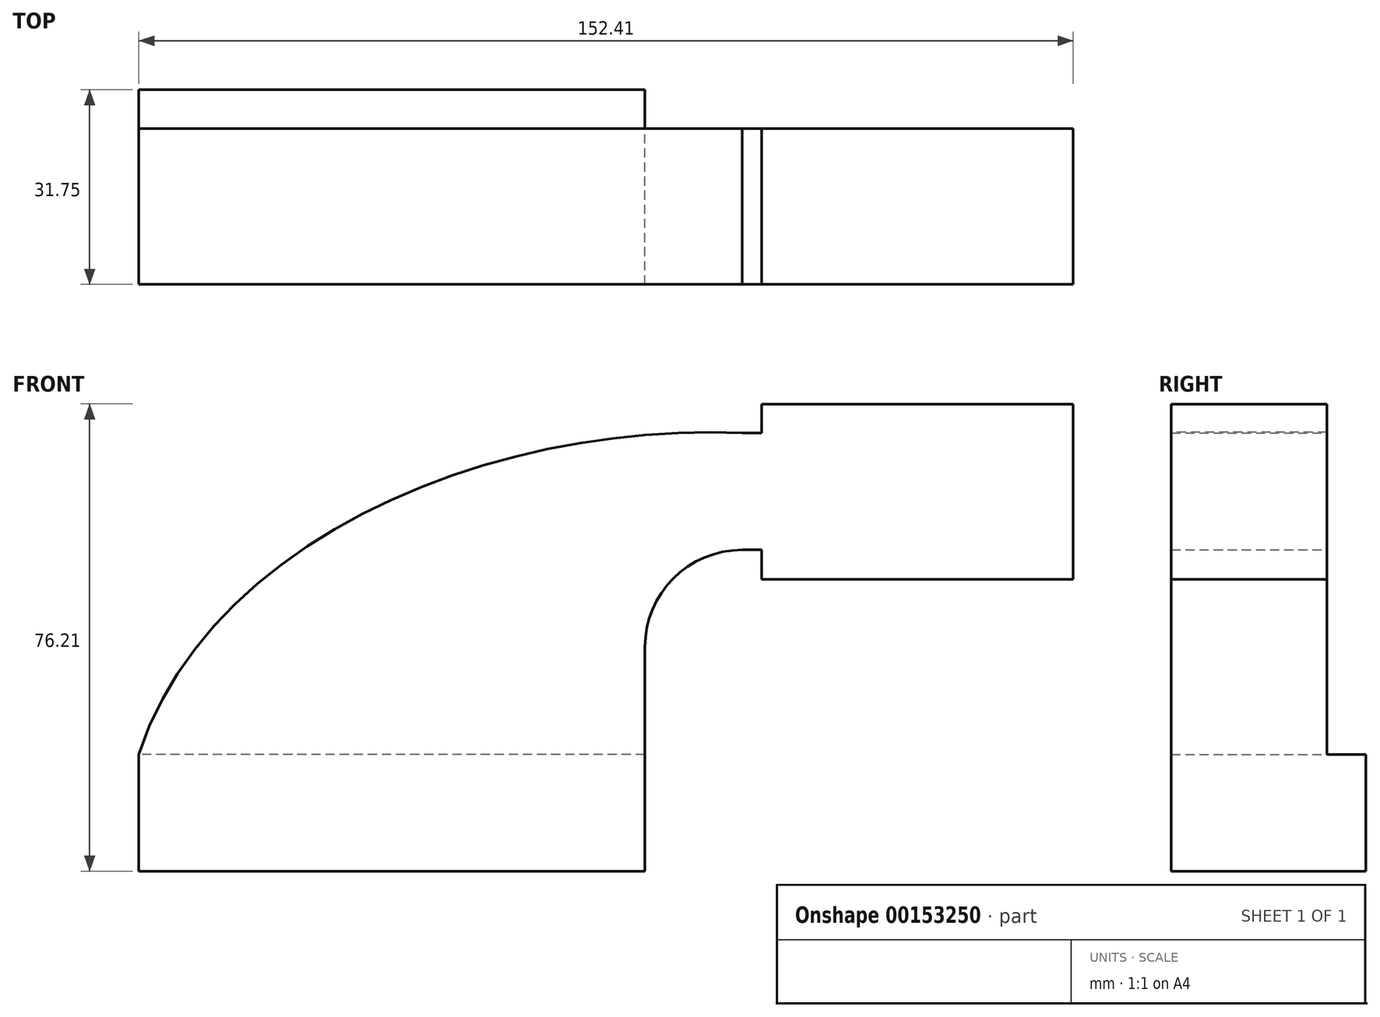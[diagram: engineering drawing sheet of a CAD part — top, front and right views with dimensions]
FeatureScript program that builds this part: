
annotation { "Feature Type Name" : "Feature", "Feature Type Description" : "" }
export const myFeature = defineFeature(function(context is Context, id is Id, definition is map)
    precondition{}
    {
        {
            var Q0;
            Q0=qCreatedBy(makeId("Front.planeOp"),FACE);
            var sketch = newSketch(context, id + "F0", { "sketchPlane" : qUnion([Q0])});
            skLineSegment(sketch, "E0.bottom", {"start": v(41.27, 9.53) * mm, "end": v(-41.28, 9.53) * mm});
            skLineSegment(sketch, "E0.top", {"start": v(41.28, -9.52) * mm, "end": v(-41.27, -9.52) * mm});
            skLineSegment(sketch, "E0.left", {"start": v(41.28, 9.53) * mm, "end": v(41.28, -9.52) * mm});
            skLineSegment(sketch, "E0.right", {"start": v(-41.28, 9.53) * mm, "end": v(-41.28, -9.52) * mm});
            skPoint(sketch, "E0.middle", {"position": v(0, 0) * mm});
            skLineSegment(sketch, "E1.bottom", {"start": v(60.32, 66.68) * mm, "end": v(111.12, 66.68) * mm});
            skLineSegment(sketch, "E1.top", {"start": v(60.33, 38.1) * mm, "end": v(111.13, 38.1) * mm});
            skLineSegment(sketch, "E1.left", {"start": v(60.32, 66.68) * mm, "end": v(60.33, 38.1) * mm});
            skLineSegment(sketch, "E1.right", {"start": v(111.13, 66.68) * mm, "end": v(111.13, 38.1) * mm});
            skPoint(sketch, "E1.middle", {"position": v(85.73, 52.39) * mm});
            skLineSegment(sketch, "E2", {"start": v(41.27, 9.53) * mm, "end": v(41.27, 27) * mm});
            skArc(sketch, "E3", {"start": v(41.27, 27) * mm, "mid": v(45.92, 38.23) * mm, "end": v(57.15, 42.88) * mm});
            skLineSegment(sketch, "E4", {"start": v(57.15, 42.88) * mm, "end": v(86.83, 42.88) * mm});
            skLineSegment(sketch, "E5.0", {"start": v(57.15, 61.93) * mm, "end": v(86.83, 61.93) * mm});
            skArc(sketch, "E5.1", {"start": v(22.23, 27) * mm, "mid": v(32.45, 51.7) * mm, "end": v(57.15, 61.93) * mm});
            skLineSegment(sketch, "E5.2", {"start": v(22.22, 9.53) * mm, "end": v(22.22, 27) * mm});
            skFitSpline(sketch, "E6", {"points": [v(-41.28, 9.52) * mm, v(57.15, 61.93) * mm], "startDerivative": vector(35.11, 107.64) * mm, "endDerivative": vector(118.61, -5.7) * mm});
            skSolve(sketch);
        }
        {
            var Q0;
            Q0=makeQuery(id+"F0.imprint","IMPRINT",FACE,{"disambiguationData":[TD([[makeQuery(id+"F0.imprint","IMPRINT",EDGE,{"derivedFrom":sQuery(id+"F0.wireOp",EDGE,"E0.top")}),-1.0]])]});
            extrude(context, id + "F1", {"entities" : qUnion([Q0]), "endBound" : BoundingType.SYMMETRIC, "depth" : 12.7 * mm});
        }
        {
            var Q0;
            Q0 = qSketchRegion(id + "F0", true);
            extrude(context, id + "F2", {"entities" : qUnion([Q0]), "operationType" : NewBodyOperationType.ADD, "depth" : 25.4 * mm});
        }
    });
